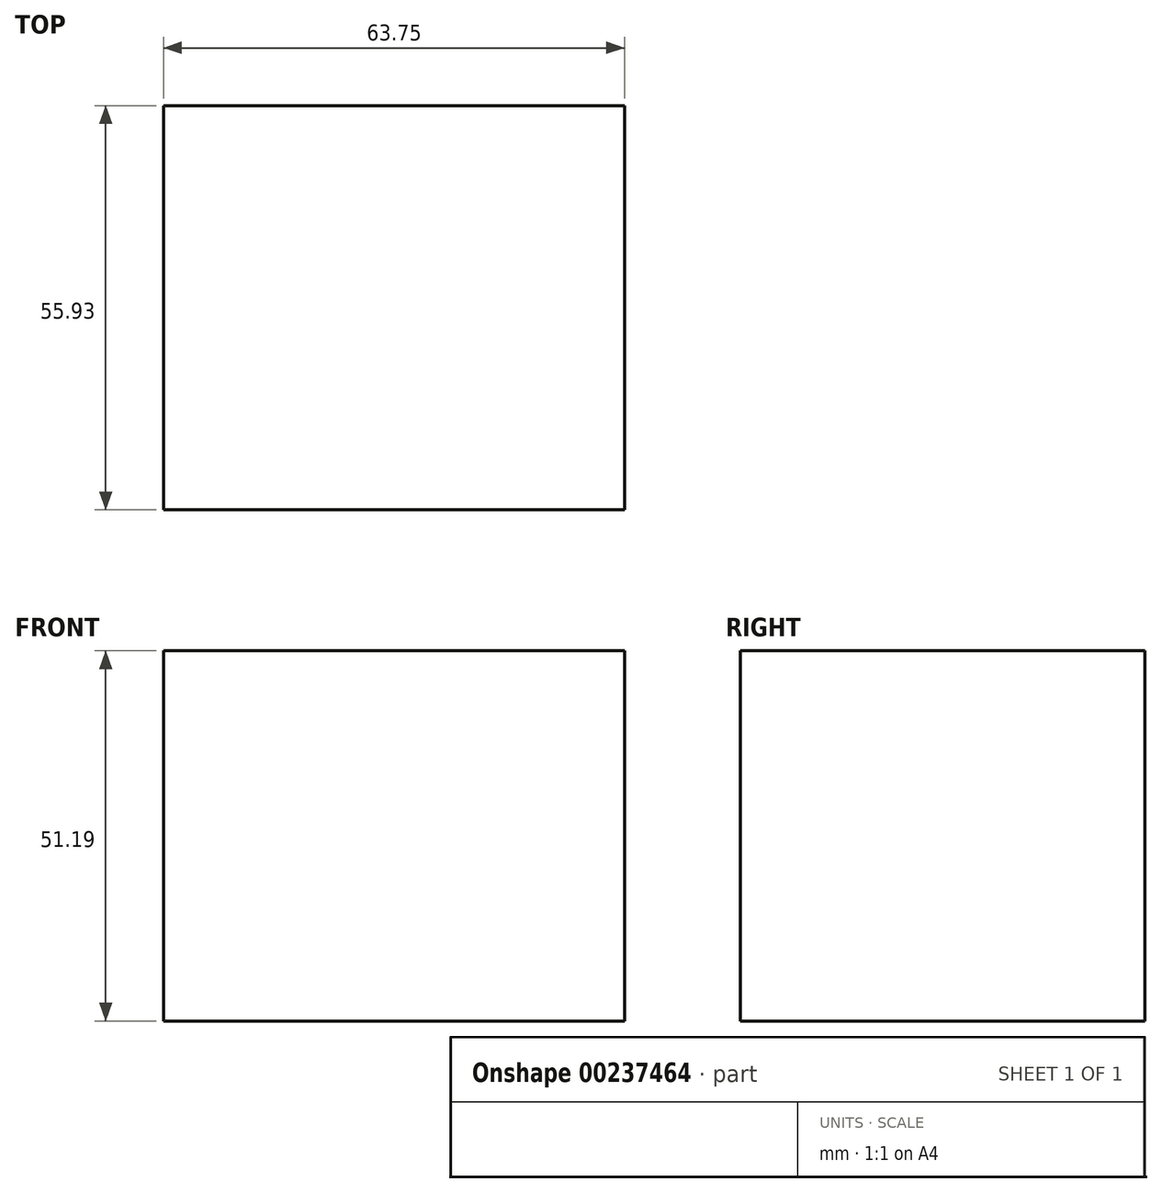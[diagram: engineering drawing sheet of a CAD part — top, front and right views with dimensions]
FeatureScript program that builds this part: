
annotation { "Feature Type Name" : "Feature", "Feature Type Description" : "" }
export const myFeature = defineFeature(function(context is Context, id is Id, definition is map)
    precondition{}
    {
        {
            var Q0;
            Q0=qCreatedBy(makeId("Right.planeOp"),FACE);
            var sketch = newSketch(context, id + "F0", { "sketchPlane" : qUnion([Q0])});
            skLineSegment(sketch, "E0.bottom", {"start": v(0, 0) * mm, "end": v(55.93, 0) * mm});
            skLineSegment(sketch, "E0.top", {"start": v(0, 51.2) * mm, "end": v(55.93, 51.2) * mm});
            skLineSegment(sketch, "E0.left", {"start": v(0, 0) * mm, "end": v(0, 51.2) * mm});
            skLineSegment(sketch, "E0.right", {"start": v(55.93, 0) * mm, "end": v(55.93, 51.2) * mm});
            skSolve(sketch);
        }
        {
            var Q0;
            Q0 = qSketchRegion(id + "F0", true);
            extrude(context, id + "F1", {"entities" : qUnion([Q0]), "depth" : 63.75 * mm});
        }
    });
